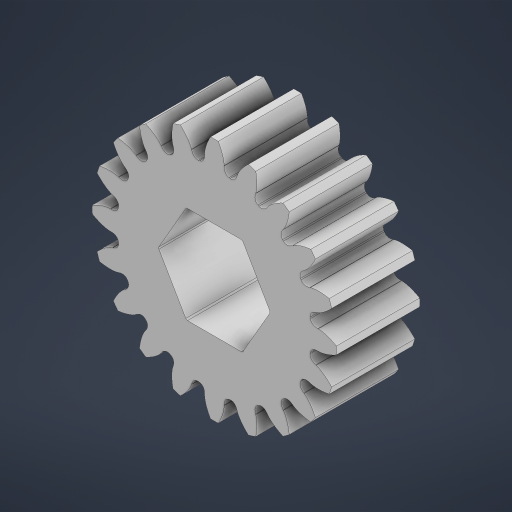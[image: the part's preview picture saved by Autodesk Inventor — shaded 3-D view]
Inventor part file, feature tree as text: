
AUTODESK INVENTOR PART (.ipt)
format: ipt  version: 2024.2 (Build 282272000, 272)  size: 1,316,352 bytes
history: native  units: in
note: dims shown in document units (in); Inventor stores cm internally (conversion verified against a paired STEP export)
features: extrude x3, sketch x3, other x2
ambient origin geometry x8: Origin, YZ Plane, XZ Plane, XY Plane, X Axis, Y Axis, Z Axis, Center Point
bodies: Solid1 (feature_tree), Solid2 (feature_tree), Solid3 (feature_tree)
feature tree (8):
  extrude  "Extrusion1"  TaperAngle=0.0deg  [1 undecoded]
  extrude  "Extrusion2"  Depth=1.0in TaperAngle=0.0deg
  extrude  "Extrusion3"  Depth=1.0in TaperAngle=0.0deg
  sketch  "Sketch1"  dims[d0=1.0in d1=0.0in d2=0.0in]
  sketch  "Sketch2"  dims[d3=0.25in d4=1.0in d5=0.0in]
  sketch  "Sketch3"  dims[d6=0.25in d7=1.0in d8=0.0in]
  other  "2806-0005-0004_91390A117_2:1"
  other  "2806-0005-0004_91390A117_3:1"
note: 1 required parameter value undecoded (feature->parameter linkage not recoverable at this tier; creation-order binding heuristic only, values carry confidence <= 0.55)
